# Revit family: BOS-15ZBud-ECON3_Familie
name_source: partatom
category: Türen
revit_build: Autodesk Revit 2017 (Build: 20160225_1515(x64)
units: mm (PartAtom-declared; Revit-internal decimal feet)

## family parameters
Basisbauteil = Wand
Beim Laden mit Abzugskörper schneiden = Nein
Gemeinsam genutzt = Nein
Immer vertikal = Ja
Raumberechnungspunkt = Ja

## types (1)
- 15ZBud ECON3
    15ZBud ECON3 = Ja
    Allgemeine Informationen zu Stahlzargen = www.BestOfSteel.de/tools-downloads/technische-infos-rund-um-die-stahlzarge/
    BBL1 Bandbezugslinie   Hinge Position 1 = 241 mm  [stored 0.790682 ft]
    BBL3 Bandbezugslinie   Hinge Position 3 = 350 mm  [stored 1.14829 ft]
    BE max. = 100 mm  [stored 0.328084 ft]
    Bauelement = BOS Stahlzarge
    Beschreibung = 2-schalige Umfassungszarge als Blockprofil ECON3, 3-teilig zerlegt
    Breite = 0 mm  [stored 0 ft]
    Dichtung 1 = Ja
    Dicke = 0 mm  [stored 0 ft]
    Doppelfalz = Nein
    Einfachfalz = Ja
    Einfügepunkt = 17 mm
    Falzaufschlag = 15 mm  [stored 0.0492126 ft]
    Falzaufschlag gesamt = 15 mm  [stored 0.0492126 ft]
    Falztiefe = 28.5 mm  [stored 0.0935039 ft]
    Falztiefe 2 = 25 mm  [stored 0.082021 ft]
    Falztiefe gesamt = 28.5 mm  [stored 0.0935039 ft]
    Funktion = Innen
    Gefälzt = Ja
    Hersteller = BOS GmbH Best Of Steel, Lütkenfelde 4, D-48282 Emsdetten
    Info-Texte sichtbar = Ja
    Information in English = Nein
    Material = grundiert, feuerverzinktes Feinblech nach DIN EN 10143
    Material - Bänder = <Nach Kategorie>
    Material - Dichtung = <Nach Kategorie>
    Material - Drückergarnitur = <Nach Kategorie>
    Material - Türblatt = <Nach Kategorie>
    Material - Unterkonstruktion = <Nach Kategorie>
    Material - Zarge = <Nach Kategorie>
    Modell = 15ZBud ECON3
    Nivellierankerabstand vorne = 0 mm  [stored 0 ft]
    Rohbaubreite = 0 mm  [stored 0 ft]
    Rohbauhöhe = 0 mm  [stored 0 ft]
    Stumpf = Nein
    Türblattabstand 1 = 1.5 mm  [stored 0.00492126 ft]
    Türblattabstand 2 = 4.5 mm  [stored 0.0147638 ft]
    Türblattabstand 3 = 4.5 mm  [stored 0.0147638 ft]
    Türblattstärke = 40 mm  [stored 0.131234 ft]
    Türblattstärke 1 = 14.5 mm  [stored 0.0475722 ft]
    Türblattstärke 2 = 25.5 mm  [stored 0.0836614 ft]
    Türblattstärke 3 = 0 mm  [stored 0 ft]
    URL = www.BestOfSteel.de/stahlzargen/zargen-fuer-drehfluegeltueren/2-schalige-stahlzargen/duo-15z-econ3/

note: [stored X ft] marks values corroborated as IEEE doubles in the binary element streams (Revit-internal decimal feet)
